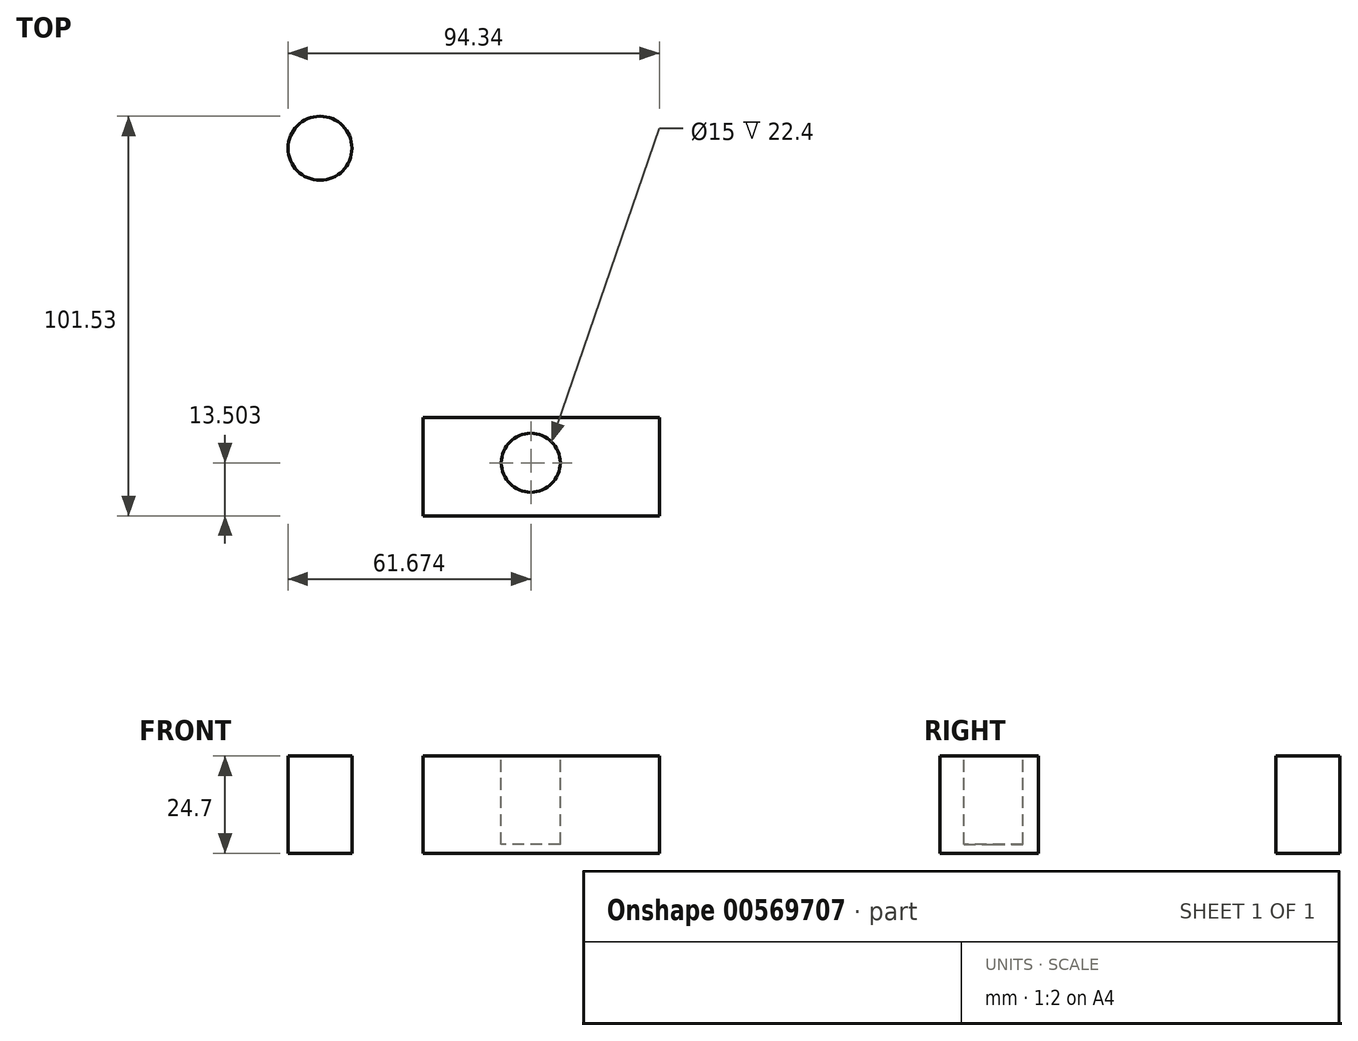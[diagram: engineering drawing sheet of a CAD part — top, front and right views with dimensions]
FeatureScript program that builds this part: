
annotation { "Feature Type Name" : "Feature", "Feature Type Description" : "" }
export const myFeature = defineFeature(function(context is Context, id is Id, definition is map)
    precondition{}
    {
        {
            var Q0;
            Q0=qCreatedBy(makeId("Top.planeOp"),FACE);
            var sketch = newSketch(context, id + "F0", { "sketchPlane" : qUnion([Q0])});
            skLineSegment(sketch, "E0.bottom", {"start": v(-35.03, -5.43) * mm, "end": v(24.97, -5.43) * mm});
            skLineSegment(sketch, "E0.top", {"start": v(-35.03, -30.43) * mm, "end": v(24.97, -30.43) * mm});
            skLineSegment(sketch, "E0.left", {"start": v(-35.03, -5.43) * mm, "end": v(-35.03, -30.43) * mm});
            skLineSegment(sketch, "E0.right", {"start": v(24.97, -5.43) * mm, "end": v(24.97, -30.43) * mm});
            skCircle(sketch, "E1", {"center": v(-61.25, 62.97) * mm, "radius": 8.12 * mm});
            skSolve(sketch);
        }
        {
            var Q0;
            Q0 = qSketchRegion(id + "F0", true);
            extrude(context, id + "F1", {"entities" : qUnion([Q0]), "depth" : 24.7 * mm, "offsetDistance" : 25 * mm});
        }
        {
            var Q0;
            Q0=makeQuery(id+"F1.opExtrude","CAP_FACE",FACE,{"disambiguationData":[OSD([sQuery(id+"F0.wireOp",EDGE,"E0.bottom"),sQuery(id+"F0.wireOp",EDGE,"E0.top"),sQuery(id+"F0.wireOp",EDGE,"E0.left"),sQuery(id+"F0.wireOp",EDGE,"E0.right")])],"isStart":false});
            var sketch = newSketch(context, id + "F2", { "sketchPlane" : qUnion([Q0])});
            skCircle(sketch, "E2", {"center": v(-7.7, -16.93) * mm, "radius": 7.5 * mm});
            skSolve(sketch);
        }
        {
            var Q0;
            Q0 = qSketchRegion(id + "F2", true);
            extrude(context, id + "F3", {"entities" : qUnion([Q0]), "operationType" : NewBodyOperationType.REMOVE, "oppositeDirection" : true, "depth" : 22.4 * mm, "offsetDistance" : 25 * mm});
        }
    });
